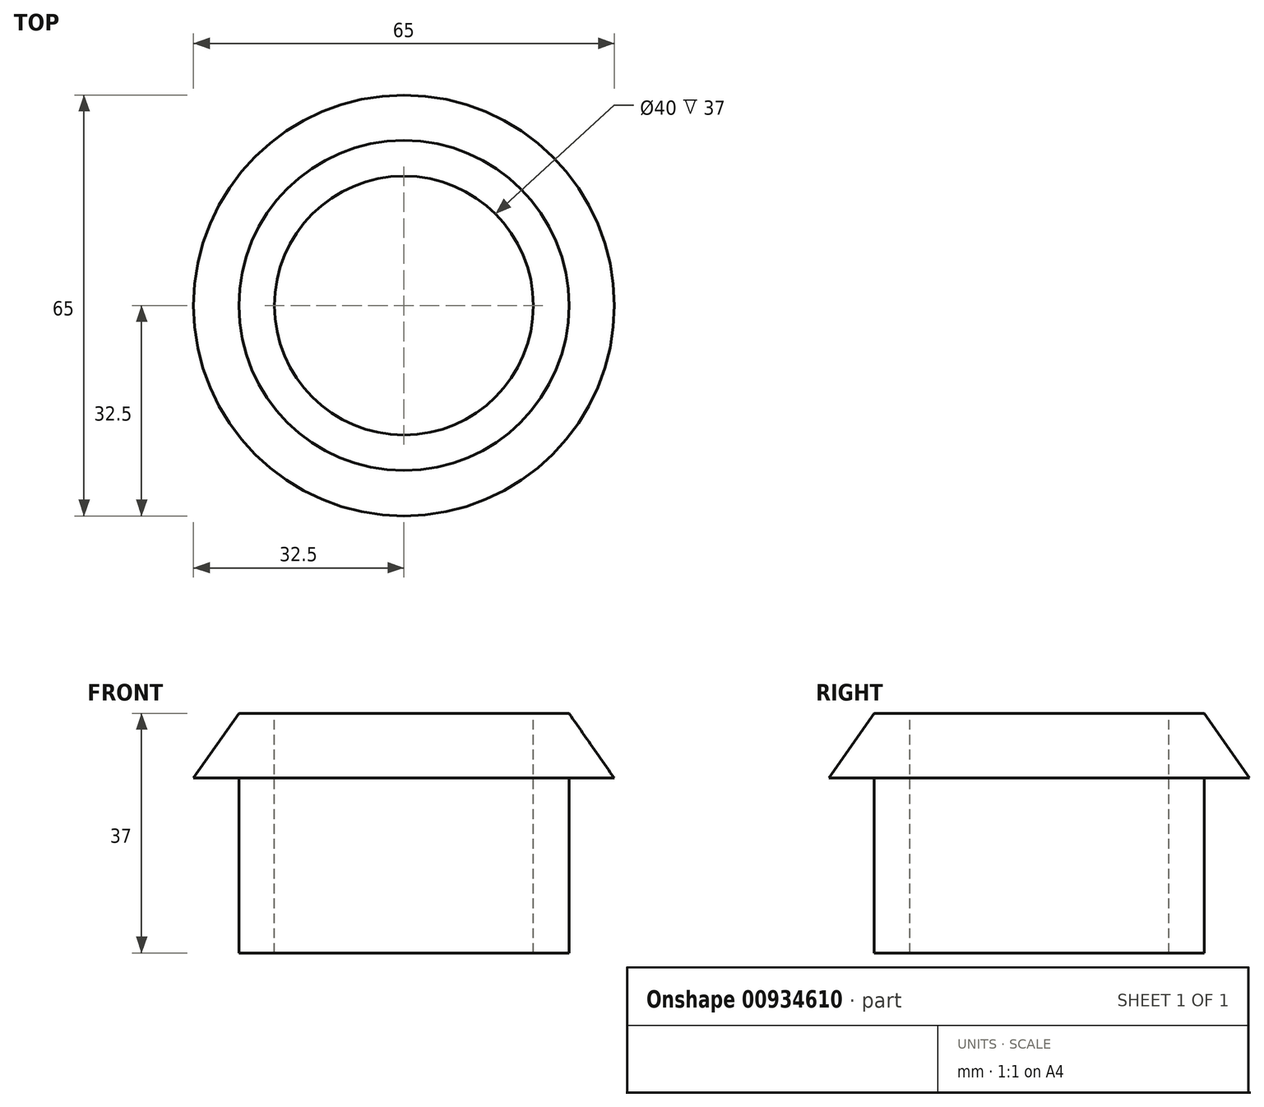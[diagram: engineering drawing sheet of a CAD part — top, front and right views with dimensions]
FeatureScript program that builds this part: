
annotation { "Feature Type Name" : "Feature", "Feature Type Description" : "" }
export const myFeature = defineFeature(function(context is Context, id is Id, definition is map)
    precondition{}
    {
        {
            var Q0;
            Q0=qCreatedBy(makeId("Front.planeOp"),FACE);
            var sketch = newSketch(context, id + "F0", { "sketchPlane" : qUnion([Q0])});
            skLineSegment(sketch, "E0.bottom", {"start": v(25.5, 13.5) * mm, "end": v(-25.5, 13.5) * mm});
            skLineSegment(sketch, "E0.top", {"start": v(25.5, -13.5) * mm, "end": v(-25.5, -13.5) * mm});
            skLineSegment(sketch, "E0.left", {"start": v(25.5, 13.5) * mm, "end": v(25.5, -13.5) * mm});
            skLineSegment(sketch, "E0.right", {"start": v(-25.5, 13.5) * mm, "end": v(-25.5, -13.5) * mm});
            skPoint(sketch, "E0.middle", {"position": v(0, 0) * mm});
            skLineSegment(sketch, "E1", {"start": v(0, 13.5) * mm, "end": v(32.5, 13.5) * mm});
            skLineSegment(sketch, "E2", {"start": v(0, 13.5) * mm, "end": v(-32.5, 13.5) * mm});
            skLineSegment(sketch, "E3.bottom", {"start": v(-25.5, 13.5) * mm, "end": v(25.5, 13.5) * mm});
            skLineSegment(sketch, "E3.top", {"start": v(-25.5, 23.5) * mm, "end": v(25.5, 23.5) * mm});
            skLineSegment(sketch, "E3.left", {"start": v(-25.5, 13.5) * mm, "end": v(-25.5, 23.5) * mm});
            skLineSegment(sketch, "E3.right", {"start": v(25.5, 13.5) * mm, "end": v(25.5, 23.5) * mm});
            skLineSegment(sketch, "E4", {"start": v(-32.5, 13.5) * mm, "end": v(-25.5, 23.5) * mm});
            skLineSegment(sketch, "E5", {"start": v(25.5, 23.5) * mm, "end": v(32.5, 13.5) * mm});
            skLineSegment(sketch, "E6.bottom", {"start": v(-20, 23.5) * mm, "end": v(19, 23.5) * mm});
            skLineSegment(sketch, "E6.top", {"start": v(-20, -13.5) * mm, "end": v(19, -13.5) * mm});
            skLineSegment(sketch, "E6.left", {"start": v(-20, 23.5) * mm, "end": v(-20, -13.5) * mm});
            skLineSegment(sketch, "E6.right", {"start": v(19, 23.5) * mm, "end": v(19, -13.5) * mm});
            skLineSegment(sketch, "E7", {"start": v(0, 23.5) * mm, "end": v(0, -13.5) * mm});
            skSolve(sketch);
        }
        {
            var Q0;
            Q0=makeQuery(id+"F0.imprint","IMPRINT",FACE,{"disambiguationData":[TD([[makeQuery(id+"F0.imprint","IMPRINT",EDGE,{"derivedFrom":sQuery(id+"F0.wireOp",EDGE,"E2")}),-1.0]])]});
            var Q1;
            {var subQ0=sQuery(id+"F0.wireOp",EDGE,"E3.left");Q1=makeQuery(id+"F0.imprint","IMPRINT",FACE,{"disambiguationData":[TD([[makeQuery(id+"F0.imprint","IMPRINT",EDGE,{"derivedFrom":subQ0}),-1.0]])]});}
            var Q2;
            {var subQ0=sQuery(id+"F0.wireOp",EDGE,"E0.right");Q2=makeQuery(id+"F0.imprint","IMPRINT",FACE,{"disambiguationData":[TD([[makeQuery(id+"F0.imprint","IMPRINT",EDGE,{"derivedFrom":subQ0}),1.0]])]});}
            var Q3;
            Q3=sQuery(id+"F0.wireOp",EDGE,"E7");
            revolve(context, id + "F1", {"surfaceOperationType" : NewSurfaceOperationType.NEW, "entities" : qUnion([Q0, Q1, Q2]), "axis" : qUnion([Q3]), "revolveType" : RevolveType.FULL});
        }
    });
